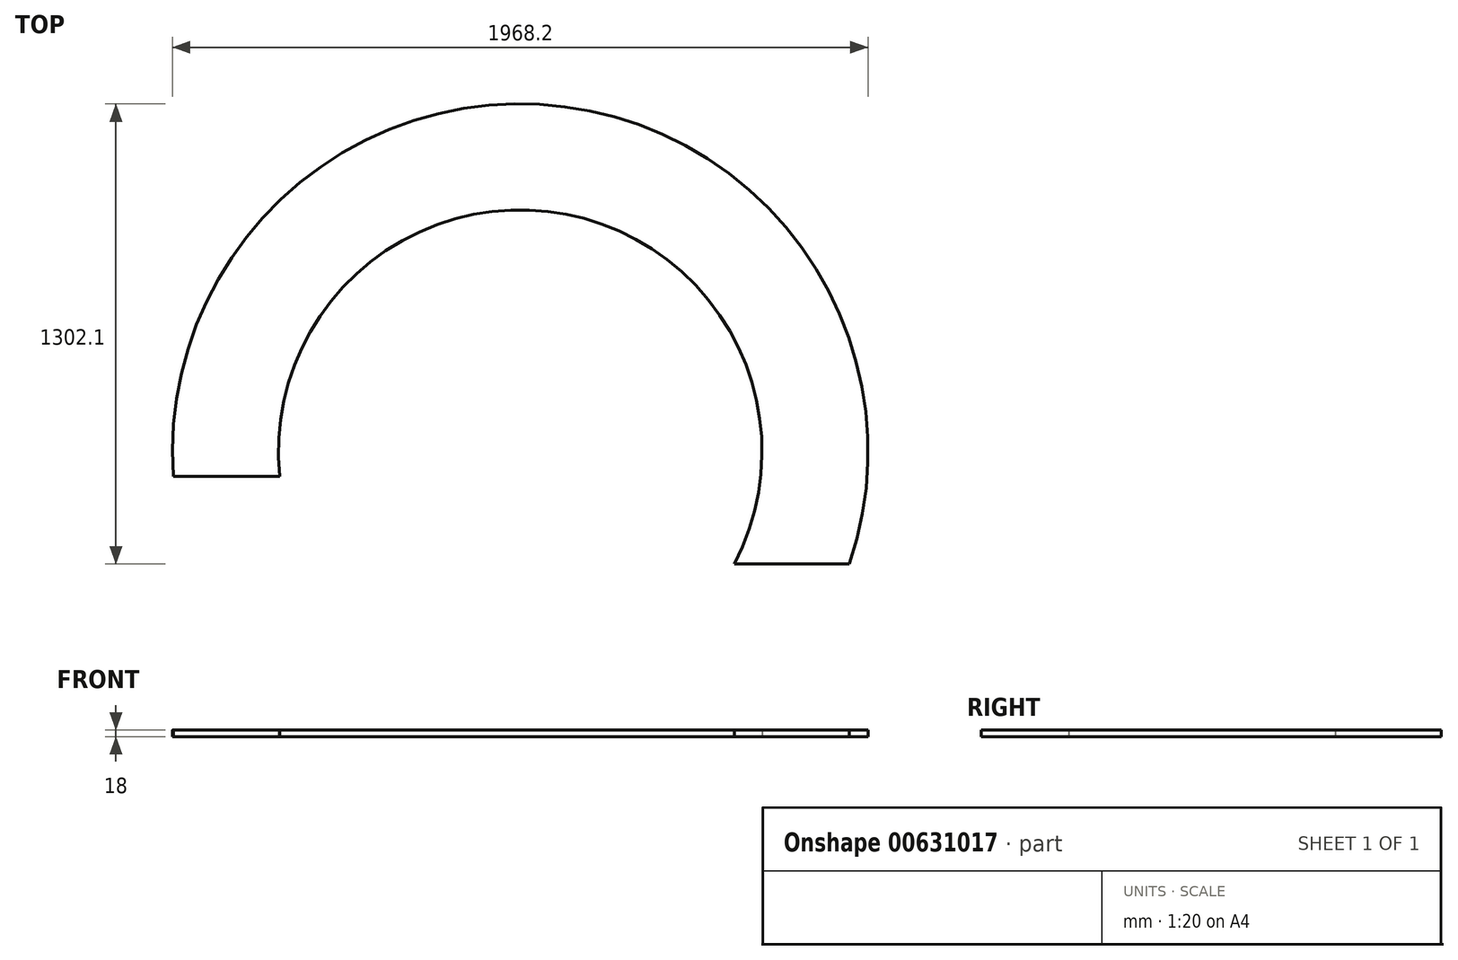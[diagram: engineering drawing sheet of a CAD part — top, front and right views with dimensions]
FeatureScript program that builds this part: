
annotation { "Feature Type Name" : "Feature", "Feature Type Description" : "" }
export const myFeature = defineFeature(function(context is Context, id is Id, definition is map)
    precondition{}
    {
        {
            var Q0;
            Q0=qCreatedBy(makeId("Top.planeOp"),FACE);
            var sketch = newSketch(context, id + "F0", { "sketchPlane" : qUnion([Q0])});
            skPoint(sketch, "E0.middle", {"position": v(0, 0) * mm});
            skPoint(sketch, "E1.end.orphan", {"position": v(-300, -300) * mm});
            skPoint(sketch, "E2.visualSharp", {"position": v(-300, 300) * mm});
            skPoint(sketch, "E3.visualSharp", {"position": v(-300, -52.1) * mm});
            skPoint(sketch, "E4.visualSharp", {"position": v(300, 300) * mm});
            skLineSegment(sketch, "E5", {"start": v(-300, -2.1) * mm, "end": v(-300, -2.1) * mm});
            skLineSegment(sketch, "E6", {"start": v(605.7, -318) * mm, "end": v(661.65, -318) * mm});
            skLineSegment(sketch, "E7", {"start": v(-680.5, -70.1) * mm, "end": v(-730.74, -70.1) * mm});
            skPoint(sketch, "E8.visualSharp", {"position": v(-300, -70.1) * mm});
            skArc(sketch, "E9.0", {"start": v(931.3, -318) * mm, "mid": v(127.45, 975.8) * mm, "end": v(-981.74, -68.13) * mm});
            skArc(sketch, "E10.0", {"start": v(624.37, -279.57) * mm, "mid": v(119.68, 673.55) * mm, "end": v(-682.46, -47.36) * mm});
            skArc(sketch, "E11", {"start": v(-682.46, -47.36) * mm, "mid": v(-681.57, -58.74) * mm, "end": v(-680.5, -70.1) * mm});
            skArc(sketch, "E12", {"start": v(624.37, -279.57) * mm, "mid": v(615.33, -298.93) * mm, "end": v(605.7, -318) * mm});
            skLineSegment(sketch, "E13", {"start": v(661.65, -318) * mm, "end": v(931.3, -318) * mm});
            skLineSegment(sketch, "E14", {"start": v(-730.74, -70.1) * mm, "end": v(-981.74, -70.1) * mm});
            skArc(sketch, "E15", {"start": v(-981.74, -68.13) * mm, "mid": v(-981.67, -69.11) * mm, "end": v(-981.6, -70.1) * mm});
            skPoint(sketch, "E16.start.orphan", {"position": v(300, -300) * mm});
            skSolve(sketch);
        }
        {
            var Q0;
            Q0=qSketchRegion(id+"F0",true);
            extrude(context, id + "F1", {"entities" : qUnion([Q0]), "depth" : 18 * mm, "offsetDistance" : 25 * mm});
        }
    });
